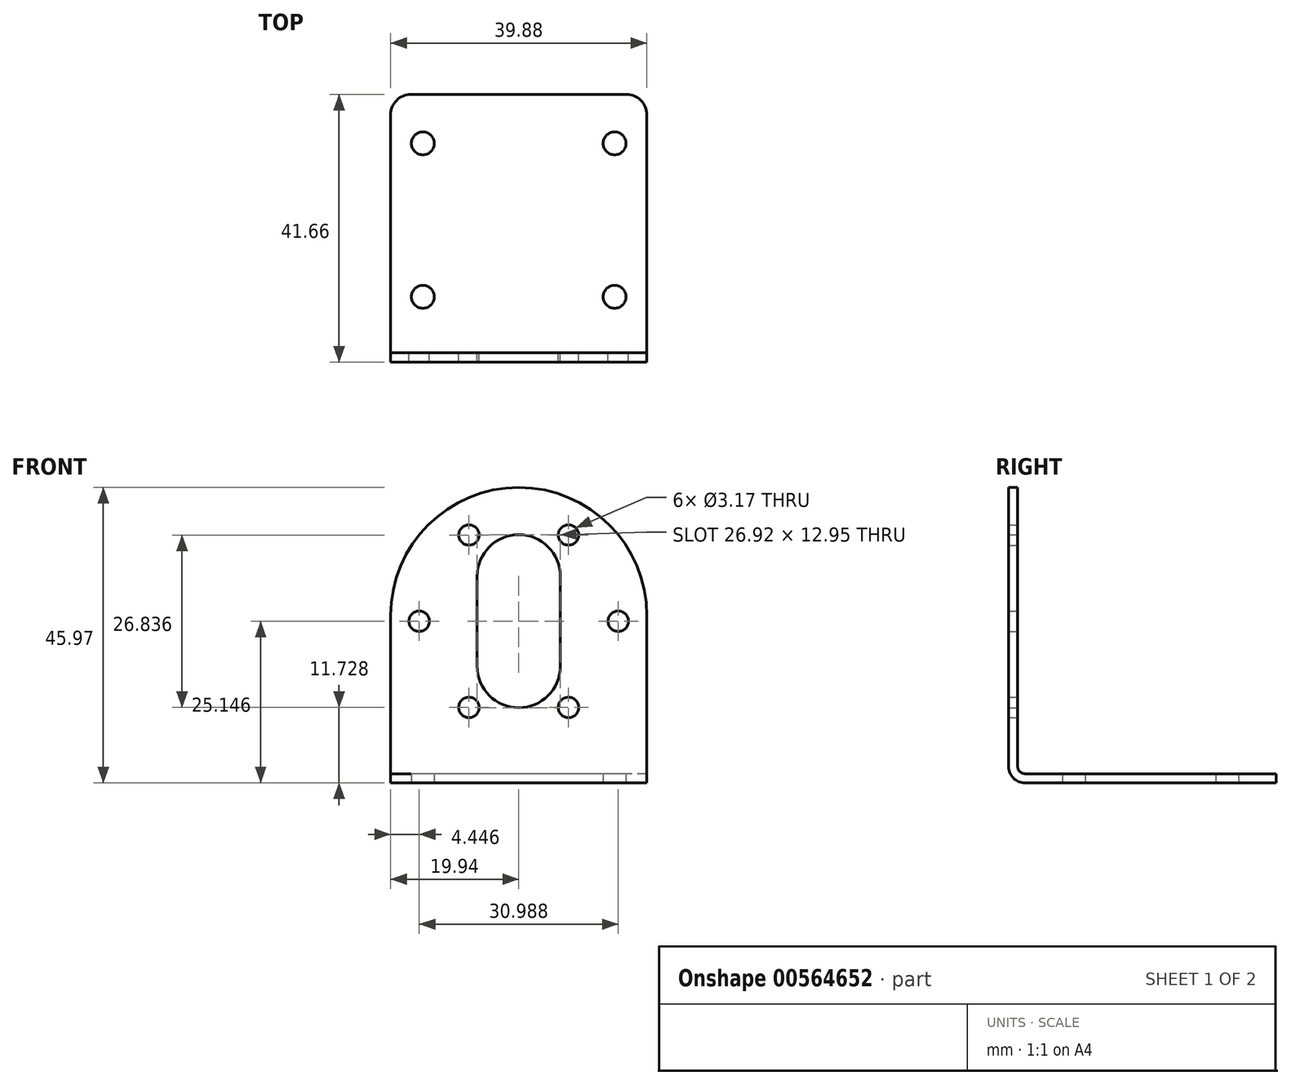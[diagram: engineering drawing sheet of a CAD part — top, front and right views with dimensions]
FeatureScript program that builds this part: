
annotation { "Feature Type Name" : "Feature", "Feature Type Description" : "" }
export const myFeature = defineFeature(function(context is Context, id is Id, definition is map)
    precondition{}
    {
        {
            var Q0;
            Q0=qCreatedBy(makeId("Right.planeOp"),FACE);
            var sketch = newSketch(context, id + "F0", { "sketchPlane" : qUnion([Q0])});
            skLineSegment(sketch, "E0", {"start": v(0, 45.97) * mm, "end": v(0, 2.54) * mm});
            skLineSegment(sketch, "E1", {"start": v(2.54, 0) * mm, "end": v(41.66, 0) * mm});
            skPoint(sketch, "E2.visualSharp", {"position": v(0, 0) * mm});
            skArc(sketch, "E2.filletArc", {"start": v(0, 2.54) * mm, "mid": v(0.74, 0.74) * mm, "end": v(2.54, 0) * mm});
            skLineSegment(sketch, "E3.0", {"start": v(2.54, 1.42) * mm, "end": v(41.66, 1.42) * mm});
            skArc(sketch, "E3.1", {"start": v(1.42, 2.54) * mm, "mid": v(1.75, 1.75) * mm, "end": v(2.54, 1.42) * mm});
            skLineSegment(sketch, "E3.2", {"start": v(1.42, 45.97) * mm, "end": v(1.42, 2.54) * mm});
            skLineSegment(sketch, "E4", {"start": v(0, 45.97) * mm, "end": v(1.42, 45.97) * mm});
            skLineSegment(sketch, "E5", {"start": v(41.66, 0) * mm, "end": v(41.66, 1.42) * mm});
            skSolve(sketch);
        }
        {
            var Q0;
            Q0 = qSketchRegion(id + "F0", true);
            extrude(context, id + "F1", {"entities" : qUnion([Q0]), "endBound" : BoundingType.SYMMETRIC, "depth" : 2540 * mm, "offsetDistance" : 25.4 * mm});
        }
        {
            var Q0;
            Q0=qCreatedBy(makeId("Front.planeOp"),FACE);
            var sketch = newSketch(context, id + "F2", { "sketchPlane" : qUnion([Q0])});
            skLineSegment(sketch, "E6", {"start": v(-19.94, 26.04) * mm, "end": v(-19.94, 0) * mm});
            skLineSegment(sketch, "E7", {"start": v(-19.94, 0) * mm, "end": v(19.94, 0) * mm});
            skLineSegment(sketch, "E8", {"start": v(19.94, 0) * mm, "end": v(19.94, 26.04) * mm});
            skArc(sketch, "E9", {"start": v(19.94, 26.04) * mm, "mid": v(0, 45.97) * mm, "end": v(-19.94, 26.04) * mm});
            skLineSegment(sketch, "E10", {"start": v(-6.48, 32.13) * mm, "end": v(-6.48, 18.16) * mm});
            skLineSegment(sketch, "E11", {"start": v(6.48, 18.16) * mm, "end": v(6.48, 32.13) * mm});
            skArc(sketch, "E12", {"start": v(6.48, 32.13) * mm, "mid": v(0, 38.6) * mm, "end": v(-6.48, 32.13) * mm});
            skArc(sketch, "E13", {"start": v(-6.48, 18.16) * mm, "mid": v(0, 11.68) * mm, "end": v(6.48, 18.16) * mm});
            skLineSegment(sketch, "E14", {"start": v(0, 32.13) * mm, "end": v(0, 18.16) * mm, "construction": true});
            skCircle(sketch, "E15.cCircle", {"center": v(0, 25.15) * mm, "radius": 15.5 * mm, "construction": true});
            skLineSegment(sketch, "E15.0", {"start": v(-15.5, 25.15) * mm, "end": v(-7.75, 38.56) * mm, "construction": true});
            skLineSegment(sketch, "E15.1", {"start": v(-7.75, 38.56) * mm, "end": v(7.75, 38.56) * mm, "construction": true});
            skLineSegment(sketch, "E15.2", {"start": v(7.75, 38.56) * mm, "end": v(15.5, 25.15) * mm, "construction": true});
            skLineSegment(sketch, "E15.3", {"start": v(15.5, 25.15) * mm, "end": v(7.75, 11.73) * mm, "construction": true});
            skLineSegment(sketch, "E15.4", {"start": v(7.75, 11.73) * mm, "end": v(-7.75, 11.73) * mm, "construction": true});
            skLineSegment(sketch, "E15.5", {"start": v(-7.75, 11.73) * mm, "end": v(-15.5, 25.15) * mm, "construction": true});
            skCircle(sketch, "E16", {"center": v(-15.5, 25.15) * mm, "radius": 1.59 * mm});
            skCircle(sketch, "E17", {"center": v(-7.75, 38.56) * mm, "radius": 1.59 * mm});
            skCircle(sketch, "E18", {"center": v(7.75, 38.56) * mm, "radius": 1.59 * mm});
            skCircle(sketch, "E19", {"center": v(15.5, 25.15) * mm, "radius": 1.59 * mm});
            skCircle(sketch, "E20", {"center": v(7.75, 11.73) * mm, "radius": 1.59 * mm});
            skCircle(sketch, "E21", {"center": v(-7.75, 11.73) * mm, "radius": 1.59 * mm});
            skSolve(sketch);
        }
        {
            var Q0;
            Q0=makeQuery(id+"F2.imprint","IMPRINT",FACE,{"disambiguationData":[TD([[makeQuery(id+"F2.imprint","IMPRINT",EDGE,{"derivedFrom":sQuery(id+"F2.wireOp",EDGE,"E6")}),1.0]])]});
            extrude(context, id + "F3", {"entities" : qUnion([Q0]), "operationType" : NewBodyOperationType.INTERSECT, "endBound" : BoundingType.SYMMETRIC, "depth" : 2540 * mm, "offsetDistance" : 25.4 * mm});
        }
        {
            var Q0;
            Q0=qCreatedBy(makeId("Top.planeOp"),FACE);
            var sketch = newSketch(context, id + "F4", { "sketchPlane" : qUnion([Q0])});
            skLineSegment(sketch, "E22", {"start": v(-19.94, 0) * mm, "end": v(-19.94, 38.48) * mm});
            skLineSegment(sketch, "E23", {"start": v(-16.76, 41.66) * mm, "end": v(16.76, 41.66) * mm});
            skLineSegment(sketch, "E24", {"start": v(19.94, 38.48) * mm, "end": v(19.94, 0) * mm});
            skLineSegment(sketch, "E25", {"start": v(19.94, 0) * mm, "end": v(-19.94, 0) * mm});
            skCircle(sketch, "E26", {"center": v(-14.92, 34.04) * mm, "radius": 1.78 * mm});
            skCircle(sketch, "E27", {"center": v(14.92, 34.04) * mm, "radius": 1.78 * mm});
            skCircle(sketch, "E28", {"center": v(-14.92, 10.16) * mm, "radius": 1.78 * mm});
            skCircle(sketch, "E29", {"center": v(14.92, 10.16) * mm, "radius": 1.78 * mm});
            skLineSegment(sketch, "E30", {"start": v(-14.92, 10.16) * mm, "end": v(14.92, 10.16) * mm, "construction": true});
            skPoint(sketch, "E31", {"position": v(0, 10.16) * mm});
            skPoint(sketch, "E32.visualSharp", {"position": v(-19.94, 41.66) * mm});
            skArc(sketch, "E32.filletArc", {"start": v(-16.76, 41.66) * mm, "mid": v(-19, 40.73) * mm, "end": v(-19.94, 38.48) * mm});
            skPoint(sketch, "E33.visualSharp", {"position": v(19.94, 41.66) * mm});
            skArc(sketch, "E33.filletArc", {"start": v(19.94, 38.48) * mm, "mid": v(19, 40.73) * mm, "end": v(16.76, 41.66) * mm});
            skSolve(sketch);
        }
        {
            var Q0;
            Q0 = qSketchRegion(id + "F4", true);
            extrude(context, id + "F5", {"entities" : qUnion([Q0]), "operationType" : NewBodyOperationType.INTERSECT, "endBound" : BoundingType.SYMMETRIC, "depth" : 2540 * mm, "offsetDistance" : 25.4 * mm});
        }
    });
